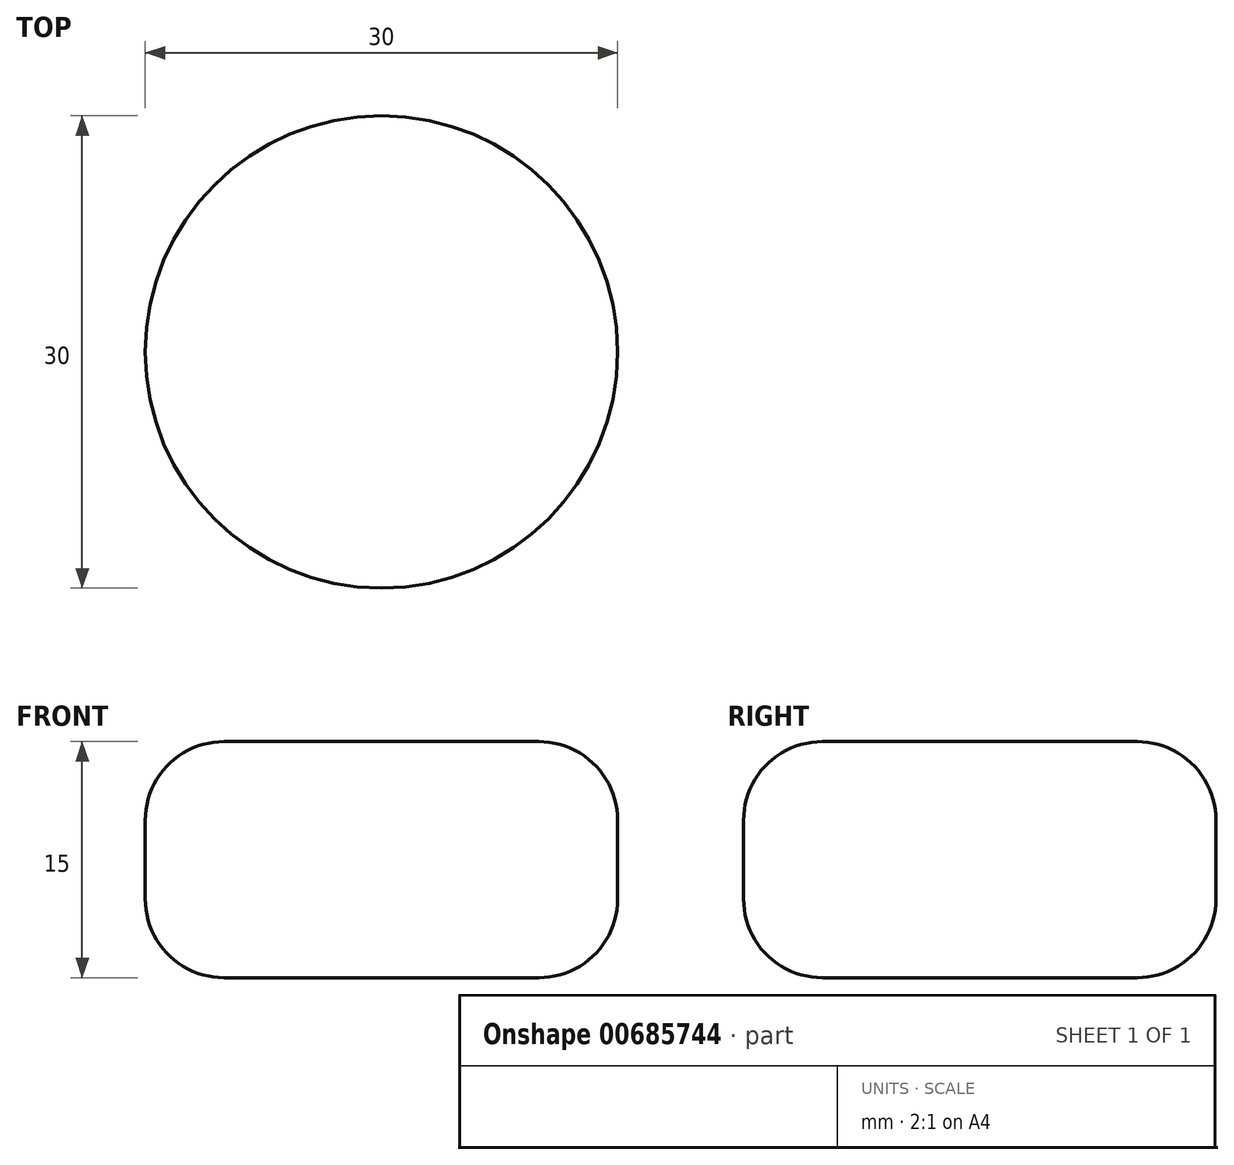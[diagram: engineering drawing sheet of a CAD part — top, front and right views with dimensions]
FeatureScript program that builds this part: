
annotation { "Feature Type Name" : "Feature", "Feature Type Description" : "" }
export const myFeature = defineFeature(function(context is Context, id is Id, definition is map)
    precondition{}
    {
        {
            var Q0;
            Q0=qCreatedBy(makeId("Top.planeOp"),FACE);
            var sketch = newSketch(context, id + "F0", { "sketchPlane" : qUnion([Q0])});
            skCircle(sketch, "E0", {"center": v(0, 0) * mm, "radius": 15 * mm});
            skSolve(sketch);
        }
        {
            var Q0;
            Q0=qSketchRegion(id+"F0",true);
            extrude(context, id + "F1", {"entities" : qUnion([Q0]), "depth" : 15 * mm, "offsetDistance" : 25 * mm});
        }
        {
            var Q0;
            Q0=makeQuery(id+"F1.opExtrude","CAP_EDGE",EDGE,{"disambiguationData":[OSD([sQuery(id+"F0.wireOp",EDGE,"E0")])],"isStart":true});
            var Q1;
            Q1=makeQuery(id+"F1.opExtrude","CAP_EDGE",EDGE,{"disambiguationData":[OSD([sQuery(id+"F0.wireOp",EDGE,"E0")])],"isStart":false});
            fillet(context, id + "F2", {"entities" : qUnion([Q0, Q1]), "radius" : 5 * mm, "tangentPropagation" : true, "allowEdgeOverflow" : false});
        }
    });
